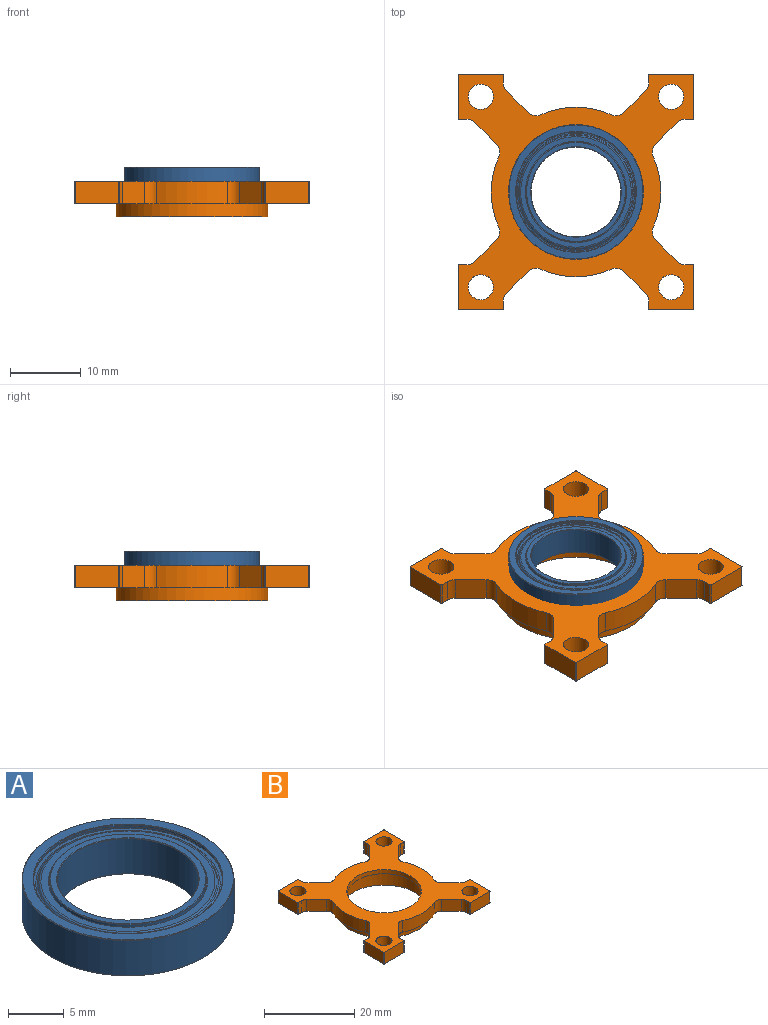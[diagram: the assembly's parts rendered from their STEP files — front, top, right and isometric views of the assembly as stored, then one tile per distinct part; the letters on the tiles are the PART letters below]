
ASSEMBLY  parts=2 mates=1
PART A: 36 faces, bbox 19.1x19.1x4 mm
  f0: cone r=6.35mm half-angle=45deg, axis (0,0,-1), area 2.9mm2, adj f22,f27
  f1: cone r=6.99mm half-angle=45deg, axis (0,0,1), area 3.2mm2, adj f20,f27
  f2: cone r=8.48mm half-angle=45deg, axis (0,0,-1), area 3.8mm2, adj f21,f28
  f3: cone r=9.47mm half-angle=45deg, axis (0,0,1), area 4.3mm2, adj f23,f28
  f4: cone r=9.53mm half-angle=45deg, axis (0,0,-1), area 4.3mm2, adj f23,f26
  f5: cone r=8.53mm half-angle=45deg, axis (0,0,1), area 3.8mm2, adj f19,f26
  f6: cone r=7.04mm half-angle=45deg, axis (0,0,-1), area 3.2mm2, adj f18,f29
  f7: cone r=6.4mm half-angle=45deg, axis (0,0,1), area 2.9mm2, adj f22,f29
  f8: cylinder r=7.15mm len=14.31mm, axis (0,0,1), area 11.4mm2, adj f24,f35
  f9: cylinder r=7.15mm len=14.31mm, axis (0,0,-1), area 11.4mm2, adj f25,f34
  f10: torus R=7.82mm, axis (0,0,1), area 9.9mm2, adj f15,f24
  f11: torus R=8.29mm, axis (0,0,1), area 10.3mm2, adj f15,f32
  f12: torus R=8.29mm, axis (0,0,-1), area 10.3mm2, adj f14,f31
  f13: torus R=7.82mm, axis (0,0,-1), area 9.9mm2, adj f14,f25
  f14: cone r=7.93mm half-angle=45deg, axis (0,0,1), area 7.5mm2, adj f12,f13
  f15: cone r=8.18mm half-angle=45deg, axis (0,0,-1), area 7.5mm2, adj f10,f11
  f16: cylinder r=8.61mm len=17.22mm, axis (0,0,1), area 13.7mm2, adj f32,f33
  f17: cylinder r=8.61mm len=17.22mm, axis (0,0,-1), area 13.7mm2, adj f30,f31
  f18: cylinder r=7.04mm len=14.07mm, axis (0,0,1), area 20.2mm2, adj f6,f35
  f19: cylinder r=8.48mm len=16.97mm, axis (0,0,1), area 10.8mm2, adj f5,f33
  f20: cylinder r=7.04mm len=14.07mm, axis (0,0,-1), area 20.2mm2, adj f1,f34
  f21: cylinder r=8.48mm len=16.97mm, axis (0,0,-1), area 10.8mm2, adj f2,f30
  f22: cylinder r=6.35mm len=12.7mm, axis (0,0,1), area 154.3mm2, adj f0,f7
  f23: cylinder r=9.53mm len=19.05mm, axis (0,0,1), area 231.4mm2, adj f3,f4
  f24: plane 15.65x15.65mm, normal (0,0,1), area 31.5mm2, adj f8,f10
  f25: plane 15.65x15.65mm, normal (0,0,-1), area 31.5mm2, adj f9,f13
  f26: plane 18.95x18.95mm, normal (0,0,1), area 53.2mm2, adj f4,f5
  f27: plane 13.97x13.97mm, normal (0,0,-1), area 24.6mm2, adj f0,f1
  f28: plane 18.95x18.95mm, normal (0,0,-1), area 53.2mm2, adj f2,f3
  f29: plane 13.97x13.97mm, normal (0,0,1), area 24.6mm2, adj f6,f7
  f30: plane 17.22x17.22mm, normal (0,0,1), area 6.8mm2, adj f17,f21
  f31: plane 17.22x17.22mm, normal (0,0,-1), area 17.2mm2, adj f12,f17
  f32: plane 17.22x17.22mm, normal (0,0,1), area 17.2mm2, adj f11,f16
  f33: plane 17.22x17.22mm, normal (0,0,-1), area 6.8mm2, adj f16,f19
  f34: plane 14.31x14.31mm, normal (0,0,-1), area 5.2mm2, adj f9,f20
  f35: plane 14.31x14.31mm, normal (0,0,1), area 5.2mm2, adj f8,f18
PART B: 67 faces, bbox 33.3x33.3x5.1 mm
  f0: cylinder r=8.26mm len=16.51mm, axis (0,0,-1), area 58mm2, adj f38,f66
  f1: cylinder r=9.53mm len=19.05mm, axis (0,0,1), area 237.1mm2, adj f65,f66
  f2: cylinder r=10.73mm len=21.46mm, axis (0,0,1), area 128.5mm2, adj f10,f65
  f3: cylinder r=1.59mm len=3.18mm, axis (0,0,1), area 6.1mm2, adj f10,f23,f24,f38
  f4: cylinder r=1.59mm len=3.18mm, axis (0,0,1), area 6.1mm2, adj f10,f22,f23,f38
  f5: cylinder r=1.78mm len=3.56mm, axis (0,0,-1), area 35.5mm2, adj f10,f38
  f6: cylinder r=1.78mm len=3.56mm, axis (0,0,-1), area 35.5mm2, adj f10,f38
  f7: cylinder r=1.78mm len=3.56mm, axis (0,0,-1), area 35.5mm2, adj f10,f38
  f8: cylinder r=1.78mm len=3.56mm, axis (0,0,-1), area 35.5mm2, adj f10,f38
  f9: cylinder r=12mm len=9.95mm, axis (0,0,1), area 32.6mm2, adj f10,f38,f61,f62
  f10: plane 33.27x33.27mm, normal (0,0,-1), area 323.2mm2, adj f2,f3,f4,f5,f6,f7,f8,f9
  f11: plane 3.18x1.08mm, normal (1,0,0), area 3.4mm2, adj f10,f38,f48,f54
  f12: plane 6.1x3.18mm, normal (0,-1,0), area 19.4mm2, adj f10,f38,f48,f49
  f13: plane 6.1x3.18mm, normal (-1,0,0), area 19.4mm2, adj f10,f38,f49,f50
  f14: plane 3.18x1.08mm, normal (0,1,0), area 3.4mm2, adj f10,f38,f50,f53
  f15: plane 3.18x3.07mm, normal (-0.71,0.71,0), area 13.8mm2, adj f10,f38,f53,f63
  f16: cylinder r=12mm len=9.95mm, axis (0,0,1), area 32.6mm2, adj f10,f38,f63,f64
  f17: plane 3.18x3.07mm, normal (-0.71,-0.71,0), area 13.8mm2, adj f10,f38,f52,f64
  f18: plane 3.18x1.08mm, normal (0,-1,0), area 3.4mm2, adj f10,f38,f39,f52
  f19: plane 6.1x3.18mm, normal (-1,0,0), area 19.4mm2, adj f10,f38,f39,f40
  f20: plane 6.1x3.18mm, normal (0,1,0), area 19.4mm2, adj f10,f38,f40,f43
  f21: plane 3.18x1.08mm, normal (1,0,0), area 3.4mm2, adj f10,f38,f43,f51
  f22: plane 3.18x3.07mm, normal (0.71,0.71,0), area 13.8mm2, adj f4,f10,f38,f51
  f23: cylinder r=12mm len=9.95mm, axis (0,0,1), area 32.6mm2, adj f3,f4,f10,f38
  f24: plane 3.18x3.07mm, normal (-0.71,0.71,0), area 13.8mm2, adj f3,f10,f38,f58
  f25: plane 3.18x1.08mm, normal (-1,0,0), area 3.4mm2, adj f10,f38,f41,f58
  f26: plane 6.1x3.18mm, normal (0,1,0), area 19.4mm2, adj f10,f38,f41,f44
  f27: plane 6.1x3.18mm, normal (1,0,0), area 19.4mm2, adj f10,f38,f44,f45
  f28: plane 3.18x1.08mm, normal (0,-1,0), area 3.4mm2, adj f10,f38,f45,f57
  f29: plane 3.18x3.07mm, normal (0.71,-0.71,0), area 13.8mm2, adj f10,f38,f57,f59
  f30: cylinder r=12mm len=9.95mm, axis (0,0,1), area 32.6mm2, adj f10,f38,f59,f60
  f31: plane 3.18x3.07mm, normal (0.71,0.71,0), area 13.8mm2, adj f10,f38,f56,f60
  f32: plane 3.18x1.08mm, normal (0,1,0), area 3.4mm2, adj f10,f38,f46,f56
  f33: plane 6.1x3.18mm, normal (1,0,0), area 19.4mm2, adj f10,f38,f46,f47
  f34: plane 6.1x3.18mm, normal (0,-1,0), area 19.4mm2, adj f10,f38,f42,f47
  f35: plane 3.18x1.08mm, normal (-1,0,0), area 3.4mm2, adj f10,f38,f42,f55
  f36: plane 3.18x3.07mm, normal (-0.71,-0.71,0), area 13.8mm2, adj f10,f38,f55,f62
  f37: plane 3.18x3.07mm, normal (0.71,-0.71,0), area 13.8mm2, adj f10,f38,f54,f61
  f38: plane 33.27x33.27mm, normal (0,0,1), area 470.9mm2, adj f0,f3,f4,f5,f6,f7,f8,f9
  f39: cylinder r=0.13mm len=3.18mm, axis (0,0,1), area 0.6mm2, adj f10,f18,f19,f38
  f40: cylinder r=0.13mm len=3.18mm, axis (0,0,-1), area 0.6mm2, adj f10,f19,f20,f38
  f41: cylinder r=0.13mm len=3.18mm, axis (0,0,-1), area 0.6mm2, adj f10,f25,f26,f38
  f42: cylinder r=0.13mm len=3.18mm, axis (0,0,-1), area 0.6mm2, adj f10,f34,f35,f38
  f43: cylinder r=0.13mm len=3.18mm, axis (0,0,1), area 0.6mm2, adj f10,f20,f21,f38
  f44: cylinder r=0.13mm len=3.18mm, axis (0,0,1), area 0.6mm2, adj f10,f26,f27,f38
  f45: cylinder r=0.13mm len=3.18mm, axis (0,0,1), area 0.6mm2, adj f10,f27,f28,f38
  f46: cylinder r=0.13mm len=3.18mm, axis (0,0,1), area 0.6mm2, adj f10,f32,f33,f38
  f47: cylinder r=0.13mm len=3.18mm, axis (0,0,1), area 0.6mm2, adj f10,f33,f34,f38
  f48: cylinder r=0.13mm len=3.18mm, axis (0,0,1), area 0.6mm2, adj f10,f11,f12,f38
  f49: cylinder r=0.13mm len=3.18mm, axis (0,0,1), area 0.6mm2, adj f10,f12,f13,f38
  f50: cylinder r=0.13mm len=3.18mm, axis (0,0,-1), area 0.6mm2, adj f10,f13,f14,f38
  f51: cylinder r=1.59mm len=3.18mm, axis (0,0,1), area 4mm2, adj f10,f21,f22,f38
  f52: cylinder r=1.59mm len=3.18mm, axis (0,0,1), area 4mm2, adj f10,f17,f18,f38
  f53: cylinder r=1.59mm len=3.18mm, axis (0,0,1), area 4mm2, adj f10,f14,f15,f38
  f54: cylinder r=1.59mm len=3.18mm, axis (0,0,1), area 4mm2, adj f10,f11,f37,f38
  f55: cylinder r=1.59mm len=3.18mm, axis (0,0,1), area 4mm2, adj f10,f35,f36,f38
  f56: cylinder r=1.59mm len=3.18mm, axis (0,0,1), area 4mm2, adj f10,f31,f32,f38
  f57: cylinder r=1.59mm len=3.18mm, axis (0,0,1), area 4mm2, adj f10,f28,f29,f38
  f58: cylinder r=1.59mm len=3.18mm, axis (0,0,1), area 4mm2, adj f10,f24,f25,f38
  f59: cylinder r=1.59mm len=3.18mm, axis (0,0,1), area 6.1mm2, adj f10,f29,f30,f38
  f60: cylinder r=1.59mm len=3.18mm, axis (0,0,1), area 6.1mm2, adj f10,f30,f31,f38
  f61: cylinder r=1.59mm len=3.18mm, axis (0,0,1), area 6.1mm2, adj f9,f10,f37,f38
  f62: cylinder r=1.59mm len=3.18mm, axis (0,0,1), area 6.1mm2, adj f9,f10,f36,f38
  f63: cylinder r=1.59mm len=3.18mm, axis (0,0,1), area 6.1mm2, adj f10,f15,f16,f38
  f64: cylinder r=1.59mm len=3.18mm, axis (0,0,1), area 6.1mm2, adj f10,f16,f17,f38
  f65: plane 21.46x21.46mm, normal (0,0,-1), area 76.8mm2, adj f1,f2
  f66: plane 19.05x19.05mm, normal (0,0,-1), area 70.9mm2, adj f0,f1
PLACE A at identity
PLACE B at identity fixed
MATE revolute A.f1 <-> B.f9  axis (0,0,1) through (0,0,0)mm
